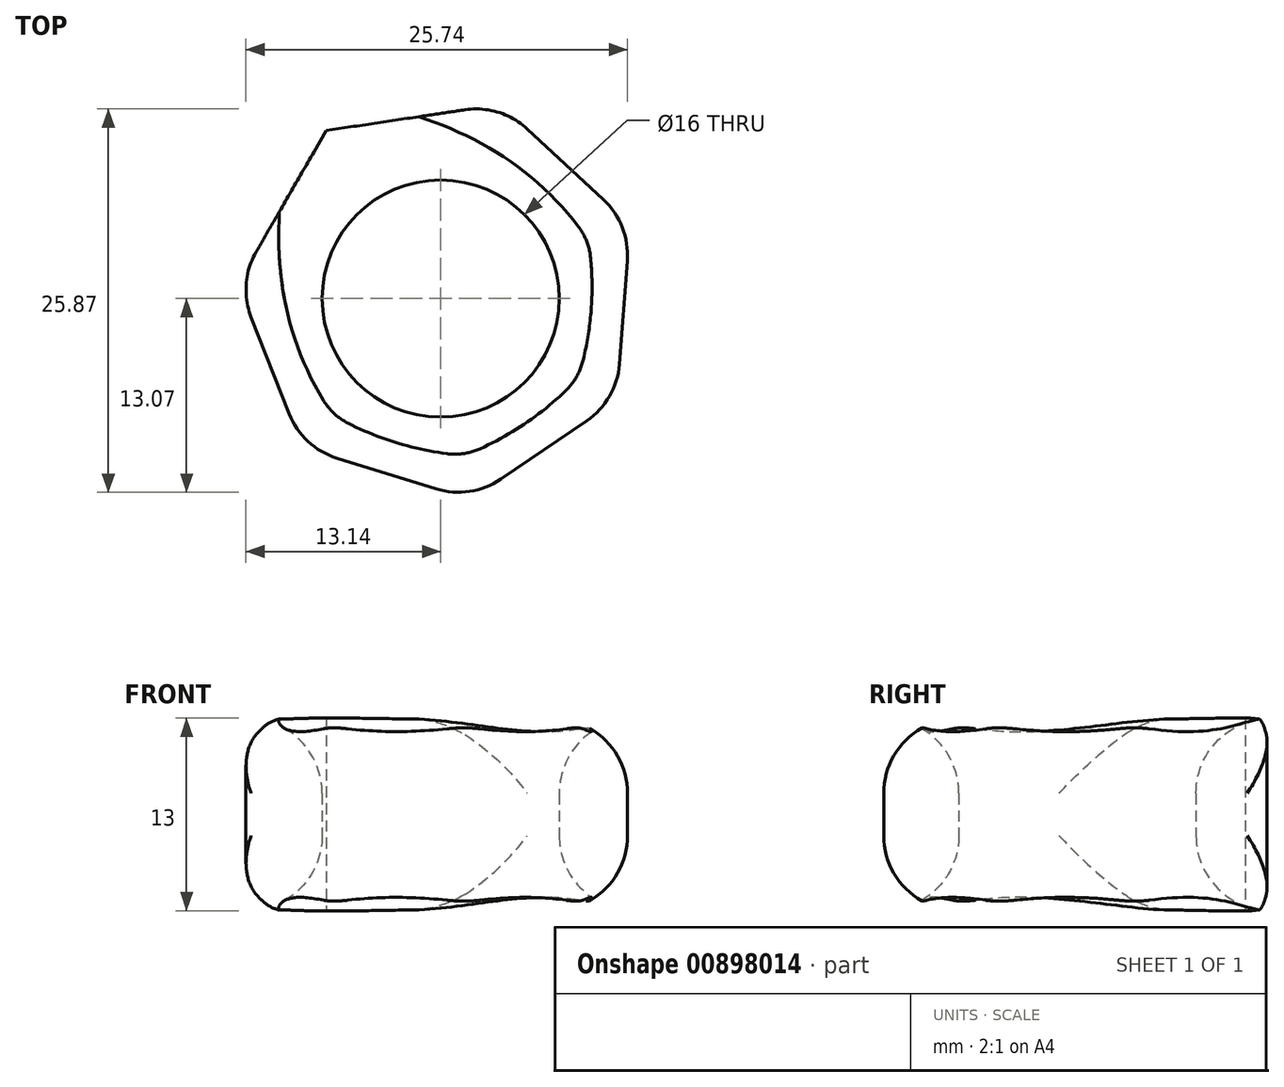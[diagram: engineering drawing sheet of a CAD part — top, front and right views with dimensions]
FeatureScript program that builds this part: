
annotation { "Feature Type Name" : "Feature", "Feature Type Description" : "" }
export const myFeature = defineFeature(function(context is Context, id is Id, definition is map)
    precondition{}
    {
        {
            var Q0;
            Q0=qCreatedBy(makeId("Top.planeOp"),FACE);
            var sketch = newSketch(context, id + "F0", { "sketchPlane" : qUnion([Q0])});
            skCircle(sketch, "E0.cCircle", {"center": v(0, 0) * mm, "radius": 12.36 * mm, "construction": true});
            skLineSegment(sketch, "E0.0", {"start": v(-13.68, 1.03) * mm, "end": v(-7.72, 11.34) * mm});
            skLineSegment(sketch, "E0.1", {"start": v(-7.72, 11.34) * mm, "end": v(4.05, 13.1) * mm});
            skLineSegment(sketch, "E0.2", {"start": v(4.05, 13.1) * mm, "end": v(12.77, 5) * mm});
            skLineSegment(sketch, "E0.3", {"start": v(12.77, 5) * mm, "end": v(11.88, -6.87) * mm});
            skLineSegment(sketch, "E0.4", {"start": v(11.88, -6.87) * mm, "end": v(2.04, -13.57) * mm});
            skLineSegment(sketch, "E0.5", {"start": v(2.04, -13.57) * mm, "end": v(-9.34, -10.05) * mm});
            skLineSegment(sketch, "E0.6", {"start": v(-9.34, -10.05) * mm, "end": v(-13.68, 1.03) * mm});
            skPoint(sketch, "E0.0.midPoint", {"position": v(-10.7, 6.19) * mm});
            skCircle(sketch, "E1", {"center": v(0, 0) * mm, "radius": 8 * mm});
            skSolve(sketch);
        }
        {
            var Q0;
            Q0 = qSketchRegion(id + "F0", true);
            extrude(context, id + "F1", {"entities" : qUnion([Q0]), "depth" : 13 * mm, "offsetDistance" : 25.4 * mm});
        }
        {
            var Q0;
            Q0=makeQuery(id+"F1.opExtrude","SWEPT_FACE",FACE,{"disambiguationData":[OSD([sQuery(id+"F0.wireOp",EDGE,"E1")])]});
            var Q1;
            Q1=makeQuery(id+"F1.opExtrude","SWEPT_FACE",FACE,{"disambiguationData":[OSD([sQuery(id+"F0.wireOp",EDGE,"E0.5")])]});
            var Q2;
            Q2=makeQuery(id+"F1.opExtrude","SWEPT_FACE",FACE,{"disambiguationData":[OSD([sQuery(id+"F0.wireOp",EDGE,"E0.4")])]});
            var Q3;
            Q3=makeQuery(id+"F1.opExtrude","SWEPT_FACE",FACE,{"disambiguationData":[OSD([sQuery(id+"F0.wireOp",EDGE,"E0.3")])]});
            var Q4;
            Q4=makeQuery(id+"F1.opExtrude","SWEPT_FACE",FACE,{"disambiguationData":[OSD([sQuery(id+"F0.wireOp",EDGE,"E0.6")])]});
            var Q5;
            Q5=makeQuery(id+"F1.opExtrude","SWEPT_FACE",FACE,{"disambiguationData":[OSD([sQuery(id+"F0.wireOp",EDGE,"E0.2")])]});
            fillet(context, id + "F2", {"entities" : qUnion([Q0, Q1, Q2, Q3, Q4, Q5]), "radius" : 5.08 * mm, "tangentPropagation" : true, "allowEdgeOverflow" : false});
        }
    });
